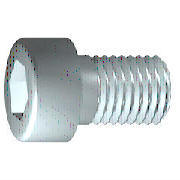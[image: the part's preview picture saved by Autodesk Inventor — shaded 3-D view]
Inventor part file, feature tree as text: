
AUTODESK INVENTOR PART (.ipt)
format: ipt  version: 2020 (Build 240168000, 168)  size: 187,904 bytes
history: native  units: mm (DEFAULTED — no unit token found)
features: sketch x2, extrude x1, plane x1, fillet x1
ambient origin geometry x7: Origin, YZ Plane, XY Plane, X Axis, Y Axis, Z Axis, Center Point
bodies: Solid1 (feature_tree), Body (feature_tree)
feature tree (5):
  extrude  "Slot"  Depth=5.0mm
  plane  "Work Plane1"
  fillet  "Fillet2"  Radius=5.0mm
  sketch  "Sketch1"  dims[d1=22.0mm d2=0.766912mm d3=5.0mm]
  sketch  "Sketch2"  dims[d4=3.8mm d5=60.0deg d6=8.0mm d7=8.0mm d8=5.773503mm d9=13.0mm d10=90.0deg d11=10.0mm d12=0.0mm d13=22.0mm d14=0.0mm d15=0.766813mm d16=0.766813mm d17=0.8mm d19=0.0mm d26=70.0mm d27=45.0deg d28=0.0mm d29=0.0mm d30=0.1mm]
